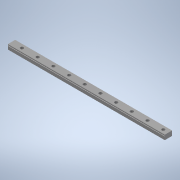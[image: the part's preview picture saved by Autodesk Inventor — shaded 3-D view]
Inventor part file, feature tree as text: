
AUTODESK INVENTOR PART (.ipt)
format: ipt  version: 2021.3 (Build 253353000, 353)  size: 137,728 bytes
history: native  units: mm
features: extrude x3, sketch x3, mirror x1, pattern_linear x1, plane x1
ambient origin geometry x8: Origin, YZ Plane, XZ Plane, XY Plane, X Axis, Y Axis, Z Axis, Center Point
bodies: Solid1 (feature_tree)
feature tree (9):
  extrude  "Extrusion1"  Depth=14.0mm
  extrude  "Extrusion2"  Depth=9.0mm
  mirror  "Mirror1"
  extrude  "Extrusion3"  Depth=9.0mm TaperAngle=0.0deg
  pattern_linear  "Rectangular Pattern1"  Spacing1=6.0mm  [1 undecoded]
  sketch  "Sketch1"  dims[d0=300.0mm d1=14.0mm]
  sketch  "Sketch2"  dims[d2=9.0mm d3=0.0mm d4=1.0mm]
  plane  "Work Plane1"
  sketch  "Sketch3"  dims[d5=2.0mm d6=9.0mm d7=0.0mm d9=6.0mm d10=20.0mm d11=9.0mm d12=0.0mm d13=100.0mm d15=30.0mm]
note: 1 required parameter value undecoded (feature->parameter linkage not recoverable at this tier; creation-order binding heuristic only, values carry confidence <= 0.55)
